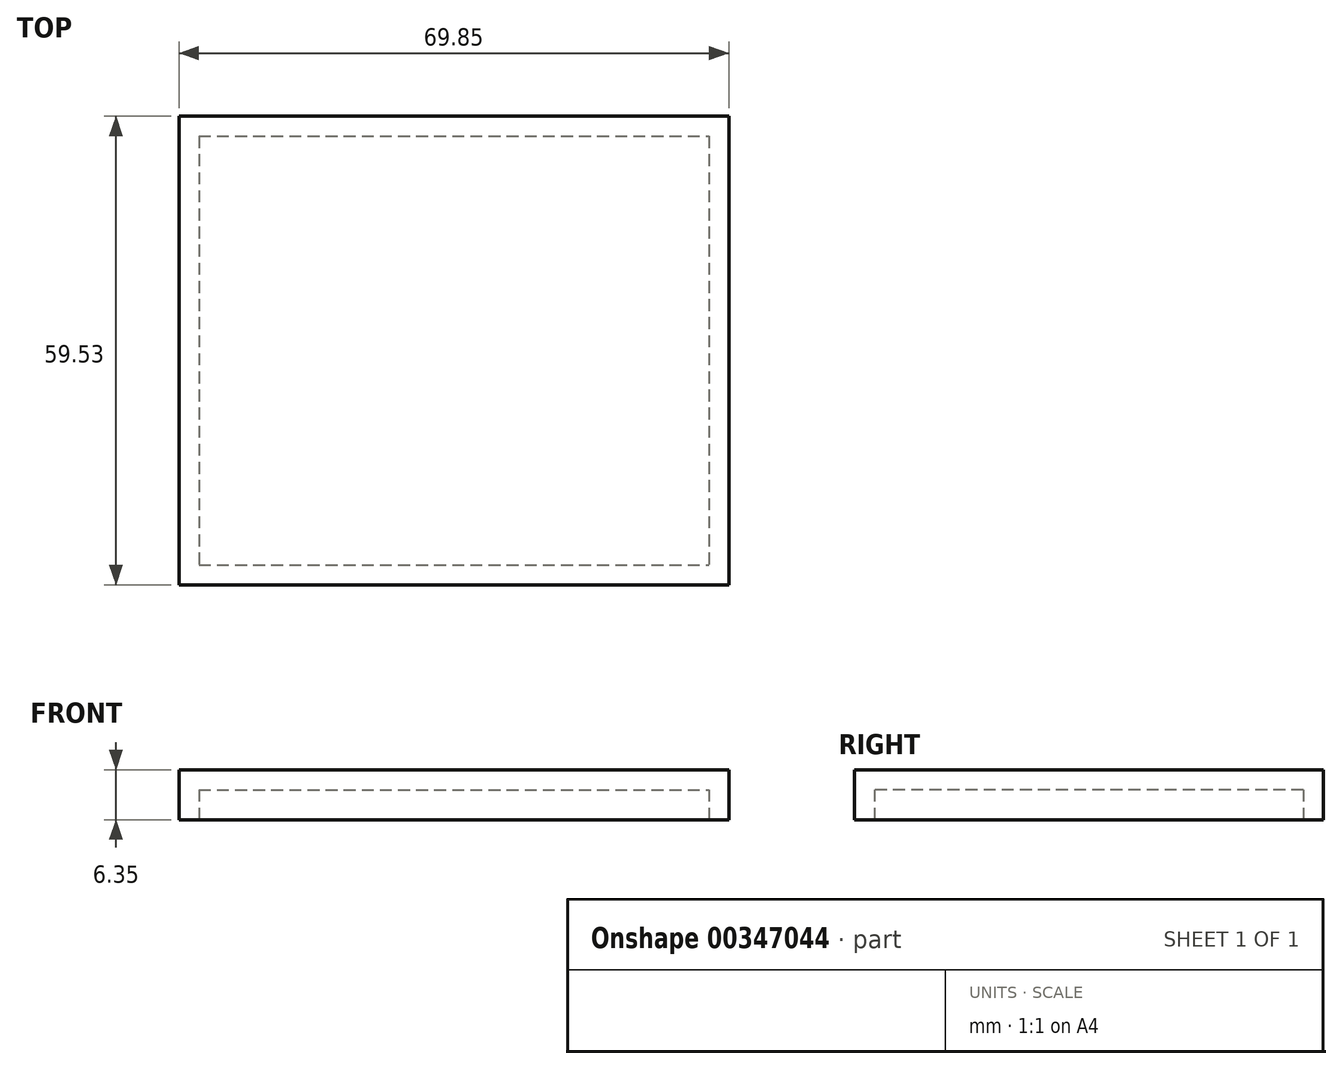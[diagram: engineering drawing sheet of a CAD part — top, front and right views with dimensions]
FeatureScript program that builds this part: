
annotation { "Feature Type Name" : "Feature", "Feature Type Description" : "" }
export const myFeature = defineFeature(function(context is Context, id is Id, definition is map)
    precondition{}
    {
        {
            var Q0;
            Q0=qCreatedBy(makeId("Top.planeOp"),FACE);
            var sketch = newSketch(context, id + "F0", { "sketchPlane" : qUnion([Q0])});
            skLineSegment(sketch, "E0.bottom", {"start": v(-39.28, 44.12) * mm, "end": v(30.57, 44.12) * mm});
            skLineSegment(sketch, "E0.top", {"start": v(-39.28, -15.41) * mm, "end": v(30.57, -15.41) * mm});
            skLineSegment(sketch, "E0.left", {"start": v(-39.28, 44.12) * mm, "end": v(-39.28, -15.41) * mm});
            skLineSegment(sketch, "E0.right", {"start": v(30.57, 44.12) * mm, "end": v(30.57, -15.41) * mm});
            skSolve(sketch);
        }
        {
            var Q0;
            Q0=makeQuery(id+"F0.imprint","IMPRINT",FACE,{"disambiguationData":[TD([[makeQuery(id+"F0.imprint","IMPRINT",EDGE,{"derivedFrom":sQuery(id+"F0.wireOp",EDGE,"E0.bottom")}),-1.0]])]});
            extrude(context, id + "F1", {"entities" : qUnion([Q0]), "depth" : 6.35 * mm});
        }
        {
            var Q0;
            Q0=makeQuery(id+"F1.opExtrude","CAP_FACE",FACE,{"disambiguationData":[OSD([sQuery(id+"F0.wireOp",EDGE,"E0.bottom"),sQuery(id+"F0.wireOp",EDGE,"E0.top"),sQuery(id+"F0.wireOp",EDGE,"E0.left"),sQuery(id+"F0.wireOp",EDGE,"E0.right")])],"isStart":true});
            shell(context, id + "F2", {"entities" : qUnion([Q0]), "thickness" : 2.54 * mm});
        }
    });
